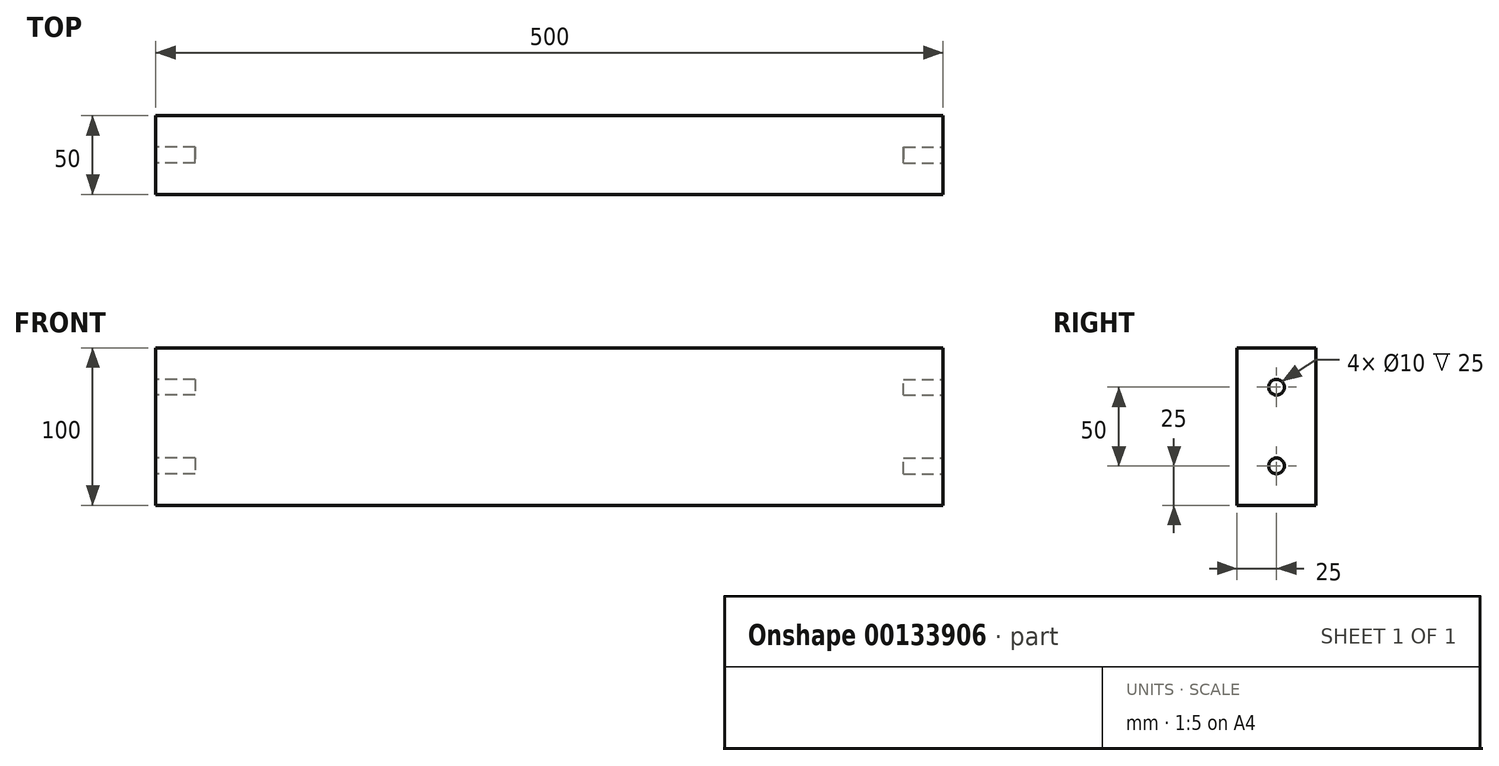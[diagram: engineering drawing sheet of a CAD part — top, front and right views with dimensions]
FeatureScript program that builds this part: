
annotation { "Feature Type Name" : "Feature", "Feature Type Description" : "" }
export const myFeature = defineFeature(function(context is Context, id is Id, definition is map)
    precondition{}
    {
        {
            var Q0;
            Q0=qCreatedBy(makeId("Front.planeOp"),FACE);
            var sketch = newSketch(context, id + "F0", { "sketchPlane" : qUnion([Q0])});
            skLineSegment(sketch, "E0.bottom", {"start": v(250, -50) * mm, "end": v(-250, -50) * mm});
            skLineSegment(sketch, "E0.top", {"start": v(250, 50) * mm, "end": v(-250, 50) * mm});
            skLineSegment(sketch, "E0.left", {"start": v(250, -50) * mm, "end": v(250, 50) * mm});
            skLineSegment(sketch, "E0.right", {"start": v(-250, -50) * mm, "end": v(-250, 50) * mm});
            skPoint(sketch, "E0.middle", {"position": v(0, 0) * mm});
            skSolve(sketch);
        }
        {
            var Q0;
            Q0=makeQuery(id+"F0.imprint","IMPRINT",FACE,{"disambiguationData":[TD([[makeQuery(id+"F0.imprint","IMPRINT",EDGE,{"derivedFrom":sQuery(id+"F0.wireOp",EDGE,"E0.bottom")}),-1.0]])]});
            extrude(context, id + "F1", {"entities" : qUnion([Q0]), "depth" : 50 * mm});
        }
        {
            var Q0;
            Q0=makeQuery(id+"F1.opExtrude","SWEPT_FACE",FACE,{"disambiguationData":[OSD([sQuery(id+"F0.wireOp",EDGE,"E0.left")])]});
            var sketch = newSketch(context, id + "F2", { "sketchPlane" : qUnion([Q0])});
            skCircle(sketch, "E1", {"center": v(-25, 25) * mm, "radius": 5 * mm});
            skPoint(sketch, "E1.centerSnap0", {"position": v(-25, 50) * mm});
            skCircle(sketch, "E2", {"center": v(-25, -25) * mm, "radius": 5 * mm});
            skPoint(sketch, "E2.centerSnap0", {"position": v(-25, -50) * mm});
            skSolve(sketch);
        }
        {
            var Q0;
            Q0=makeQuery(id+"F2.imprint","IMPRINT",FACE,{"disambiguationData":[TD([[makeQuery(id+"F2.imprint","IMPRINT",EDGE,{"derivedFrom":sQuery(id+"F2.wireOp",EDGE,"E1")}),1.0]])]});
            var Q1;
            Q1=makeQuery(id+"F2.imprint","IMPRINT",FACE,{"disambiguationData":[TD([[makeQuery(id+"F2.imprint","IMPRINT",EDGE,{"derivedFrom":sQuery(id+"F2.wireOp",EDGE,"E2")}),1.0]])]});
            extrude(context, id + "F3", {"entities" : qUnion([Q0, Q1]), "operationType" : NewBodyOperationType.REMOVE, "oppositeDirection" : true, "depth" : 25 * mm});
        }
        {
            var Q0;
            Q0=makeQuery(id+"F1.opExtrude","SWEPT_FACE",FACE,{"disambiguationData":[OSD([sQuery(id+"F0.wireOp",EDGE,"E0.right")])]});
            var sketch = newSketch(context, id + "F4", { "sketchPlane" : qUnion([Q0])});
            skCircle(sketch, "E3", {"center": v(25, 25) * mm, "radius": 5 * mm});
            skPoint(sketch, "E3.centerSnap0", {"position": v(25, 50) * mm});
            skCircle(sketch, "E4", {"center": v(25, -25) * mm, "radius": 5 * mm});
            skPoint(sketch, "E4.centerSnap0", {"position": v(25, -50) * mm});
            skSolve(sketch);
        }
        {
            var Q0;
            Q0=makeQuery(id+"F4.imprint","IMPRINT",FACE,{"disambiguationData":[TD([[makeQuery(id+"F4.imprint","IMPRINT",EDGE,{"derivedFrom":sQuery(id+"F4.wireOp",EDGE,"E3")}),1.0]])]});
            var Q1;
            Q1=makeQuery(id+"F4.imprint","IMPRINT",FACE,{"disambiguationData":[TD([[makeQuery(id+"F4.imprint","IMPRINT",EDGE,{"derivedFrom":sQuery(id+"F4.wireOp",EDGE,"E4")}),1.0]])]});
            extrude(context, id + "F5", {"entities" : qUnion([Q0, Q1]), "operationType" : NewBodyOperationType.REMOVE, "oppositeDirection" : true, "depth" : 25 * mm});
        }
    });
